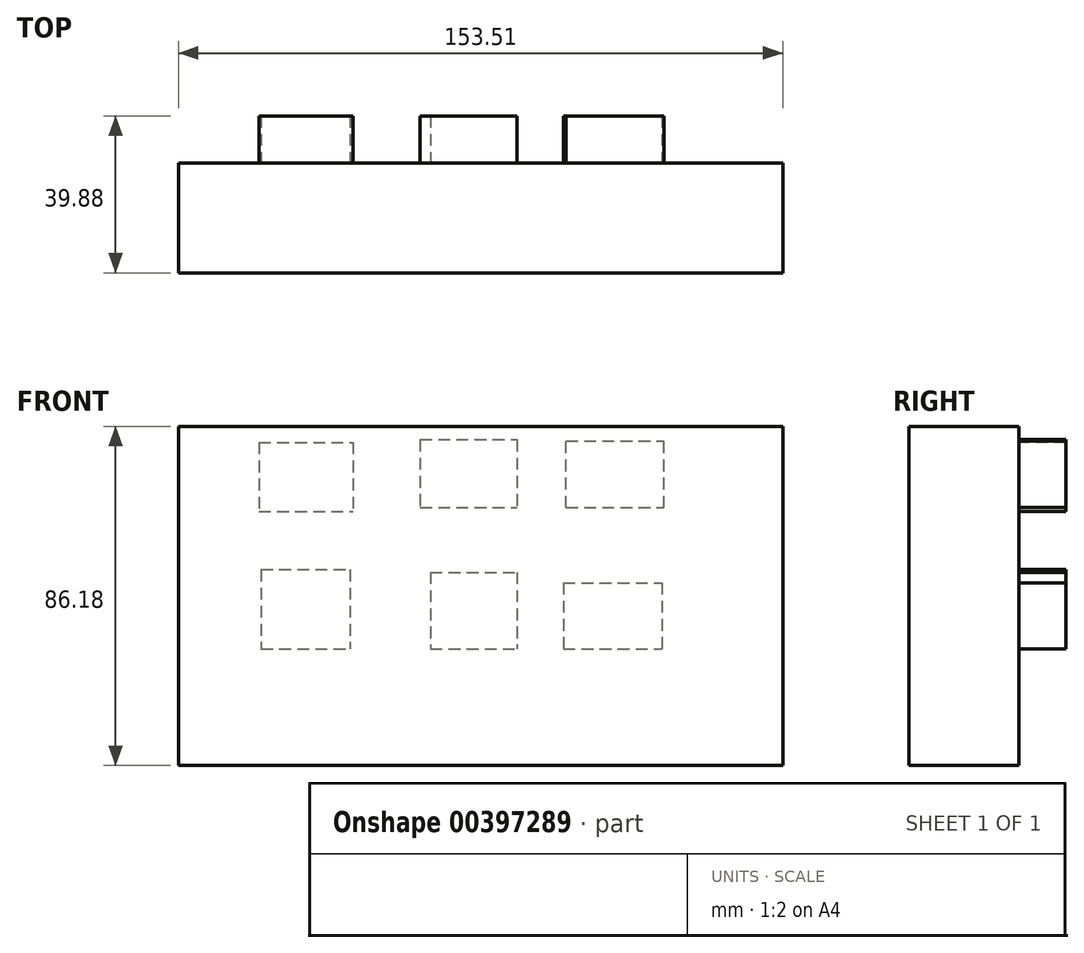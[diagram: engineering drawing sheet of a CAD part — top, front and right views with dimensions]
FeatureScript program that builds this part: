
annotation { "Feature Type Name" : "Feature", "Feature Type Description" : "" }
export const myFeature = defineFeature(function(context is Context, id is Id, definition is map)
    precondition{}
    {
        {
            var Q0;
            Q0=qCreatedBy(makeId("Front.planeOp"),FACE);
            var sketch = newSketch(context, id + "F0", { "sketchPlane" : qUnion([Q0])});
            skLineSegment(sketch, "E0.bottom", {"start": v(0, 0) * mm, "end": v(-153.5, 0) * mm});
            skLineSegment(sketch, "E0.top", {"start": v(0, 86.18) * mm, "end": v(-153.5, 86.18) * mm});
            skLineSegment(sketch, "E0.left", {"start": v(0, 0) * mm, "end": v(0, 86.18) * mm});
            skLineSegment(sketch, "E0.right", {"start": v(-153.5, 0) * mm, "end": v(-153.5, 86.18) * mm});
            skSolve(sketch);
        }
        {
            var Q0;
            Q0=makeQuery(id+"F0.imprint","IMPRINT",FACE,{"disambiguationData":[TD([[makeQuery(id+"F0.imprint","IMPRINT",EDGE,{"derivedFrom":sQuery(id+"F0.wireOp",EDGE,"E0.bottom")}),-1.0]])]});
            extrude(context, id + "F1", {"entities" : qUnion([Q0]), "depth" : 27.94 * mm});
        }
        {
            var Q0;
            Q0=qCreatedBy(makeId("Front.planeOp"),FACE);
            var sketch = newSketch(context, id + "F2", { "sketchPlane" : qUnion([Q0])});
            skLineSegment(sketch, "E1.bottom", {"start": v(-133.07, 82.1) * mm, "end": v(-109.16, 82.1) * mm});
            skLineSegment(sketch, "E1.top", {"start": v(-133.07, 64.62) * mm, "end": v(-109.16, 64.62) * mm});
            skLineSegment(sketch, "E1.left", {"start": v(-133.07, 82.1) * mm, "end": v(-133.07, 64.62) * mm});
            skLineSegment(sketch, "E1.right", {"start": v(-109.16, 82.1) * mm, "end": v(-109.16, 64.62) * mm});
            skLineSegment(sketch, "E2.bottom", {"start": v(-92.1, 82.8) * mm, "end": v(-67.46, 82.8) * mm});
            skLineSegment(sketch, "E2.top", {"start": v(-92.1, 65.56) * mm, "end": v(-67.46, 65.56) * mm});
            skLineSegment(sketch, "E2.left", {"start": v(-92.1, 82.8) * mm, "end": v(-92.1, 65.56) * mm});
            skLineSegment(sketch, "E2.right", {"start": v(-67.46, 82.8) * mm, "end": v(-67.46, 65.56) * mm});
            skLineSegment(sketch, "E3.bottom", {"start": v(-55.03, 65.56) * mm, "end": v(-30.13, 65.56) * mm});
            skLineSegment(sketch, "E3.top", {"start": v(-55.03, 82.5) * mm, "end": v(-30.13, 82.5) * mm});
            skLineSegment(sketch, "E3.left", {"start": v(-55.03, 65.56) * mm, "end": v(-55.03, 82.5) * mm});
            skLineSegment(sketch, "E3.right", {"start": v(-30.13, 65.56) * mm, "end": v(-30.13, 82.5) * mm});
            skLineSegment(sketch, "E4.bottom", {"start": v(-132.52, 49.78) * mm, "end": v(-109.92, 49.78) * mm});
            skLineSegment(sketch, "E4.top", {"start": v(-132.52, 29.6) * mm, "end": v(-109.92, 29.6) * mm});
            skLineSegment(sketch, "E4.left", {"start": v(-132.52, 49.78) * mm, "end": v(-132.52, 29.6) * mm});
            skLineSegment(sketch, "E4.right", {"start": v(-109.92, 49.78) * mm, "end": v(-109.92, 29.6) * mm});
            skLineSegment(sketch, "E5.bottom", {"start": v(-89.5, 49.12) * mm, "end": v(-67.46, 49.12) * mm});
            skLineSegment(sketch, "E5.top", {"start": v(-89.5, 29.63) * mm, "end": v(-67.46, 29.63) * mm});
            skLineSegment(sketch, "E5.left", {"start": v(-89.5, 49.12) * mm, "end": v(-89.5, 29.63) * mm});
            skLineSegment(sketch, "E5.right", {"start": v(-67.46, 49.12) * mm, "end": v(-67.46, 29.63) * mm});
            skLineSegment(sketch, "E6.bottom", {"start": v(-55.74, 46.46) * mm, "end": v(-30.69, 46.46) * mm});
            skLineSegment(sketch, "E6.top", {"start": v(-55.74, 29.63) * mm, "end": v(-30.69, 29.63) * mm});
            skLineSegment(sketch, "E6.left", {"start": v(-55.74, 46.46) * mm, "end": v(-55.74, 29.63) * mm});
            skLineSegment(sketch, "E6.right", {"start": v(-30.69, 46.46) * mm, "end": v(-30.69, 29.63) * mm});
            skSolve(sketch);
        }
        {
            var Q0;
            Q0=makeQuery(id+"F2.imprint","IMPRINT",FACE,{"disambiguationData":[TD([[makeQuery(id+"F2.imprint","IMPRINT",EDGE,{"derivedFrom":sQuery(id+"F2.wireOp",EDGE,"E4.bottom")}),-1.0]])]});
            var Q1;
            Q1=makeQuery(id+"F2.imprint","IMPRINT",FACE,{"disambiguationData":[TD([[makeQuery(id+"F2.imprint","IMPRINT",EDGE,{"derivedFrom":sQuery(id+"F2.wireOp",EDGE,"E2.bottom")}),-1.0]])]});
            var Q2;
            Q2=makeQuery(id+"F2.imprint","IMPRINT",FACE,{"disambiguationData":[TD([[makeQuery(id+"F2.imprint","IMPRINT",EDGE,{"derivedFrom":sQuery(id+"F2.wireOp",EDGE,"E5.bottom")}),-1.0]])]});
            var Q3;
            Q3=makeQuery(id+"F2.imprint","IMPRINT",FACE,{"disambiguationData":[TD([[makeQuery(id+"F2.imprint","IMPRINT",EDGE,{"derivedFrom":sQuery(id+"F2.wireOp",EDGE,"E6.bottom")}),-1.0]])]});
            var Q4;
            Q4=makeQuery(id+"F2.imprint","IMPRINT",FACE,{"disambiguationData":[TD([[makeQuery(id+"F2.imprint","IMPRINT",EDGE,{"derivedFrom":sQuery(id+"F2.wireOp",EDGE,"E3.bottom")}),1.0]])]});
            var Q5;
            Q5=makeQuery(id+"F2.imprint","IMPRINT",FACE,{"disambiguationData":[TD([[makeQuery(id+"F2.imprint","IMPRINT",EDGE,{"derivedFrom":sQuery(id+"F2.wireOp",EDGE,"E1.bottom")}),-1.0]])]});
            extrude(context, id + "F3", {"entities" : qUnion([Q0, Q1, Q2, Q3, Q4, Q5]), "operationType" : NewBodyOperationType.ADD, "oppositeDirection" : true, "depth" : 11.94 * mm});
        }
    });
